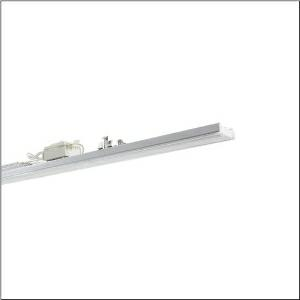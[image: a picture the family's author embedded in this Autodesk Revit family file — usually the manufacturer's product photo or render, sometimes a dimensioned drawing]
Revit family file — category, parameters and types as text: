
# Revit family: licross_21_recessed_ho_52tl12dn6e5m
name_source: partatom
category: Lighting Fixtures
units: mm (PartAtom-declared; Revit-internal decimal feet)

## family parameters
Cut with Voids When Loaded = No
Host = Face
Light Source = No
Part Type = Normal
Room Calculation Point = No
Round Connector Dimension = Use Diameter
Shared = No

## types (1)
- --- (1 x LED, 14610 lm, 84.6 W, 6500K)
    Apparent Load = 85 VA
    CIE Flux Codes = 69 91 98 100 100
    Color Rendering = 80
    Color Temperature = 6500K
    Default Elevation = 1800 mm
    Description = Licross 21 Recessed HO, luminaire insert, of sheet steel, galvanised, coil coated, white, length: 1.500mm, width: 66mm, height: 67mm, LED rated luminous flux: 14.610lm, light colour: 865, SDCM (Standard Deviation of Colour Matching)MacAdam ≤ 3 SDCM (initial), control gear: DALI 2, with plug, 5-pole, with phase selection, mains connection: 220..240V, AC, 50/60Hz, rated input power: 85W, internal wiring halogen-free, primary optical cover: cover, of PMMA, light emission: direct distribution, primary light characteristic: symmetric, protection rating (complete): IP40, insulation class (complete): insulation class I (protective earthing), certification: CE, ENEC, VDE, UKCA, protection symbol: D if used in an environment without relevant dust loads with corresponding accessories, impact resistance: IK06, permissible ambient temperature for indoor applications: -25..+30°C, corresponds to IFS (International Featured Standards) requirements for safety and quality in the food industry, reducing of maximum allowable ambient temperature of 5°C with ceiling mounting, LABS conformity tested according to VDMA 24364:2018-05, The light source and the operating device comply with the requirements of the Ecodesign Regulation (EU) 2019/2020 and are replaceable in accordance with this regulation, packaging unit: 1 piece
    Height = 58 mm
    Lamp = 1 x LED
    Lamp Light Flux = 14610 lm
    Lamp Power = 84.6 W
    Lamp count = 1
    Length = 1500 mm
    Luminous efficacy = 173 lm/W
    Manufacturer = Siteco
    ModVariant = No
    Model = 52TL12DN6E5M
    Mounting Place = Ceiling
    Mounting Type = Pendant
    Number of Poles = 1
    OnlyDefault = Yes
    Power Factor = 1
    Product Name = Licross 21 Recessed HO
    Product group = luminaire insert | ceiling pendant
    ProductGroupID = 901
    Protection Class = Protection class I
    Protection Degree = IP 40
    RLX_Detail_Level = 1
    RLX_Emergency_Light_Flux = 0 lm
    RLX_Emergency_Type = 0
    RLX_Emergency_Type_DB = No
    RlxData = <blob elided: 25001 chars, md5=13d18b7d>
    Socket = socket
    Standby Power = 0 W
    System Light Flux = 14610 lm
    System Power = 85 W
    Type Comments = factory setting: luminous flux: 100 % | dim-lin: 254 | 484 mA
    Type Image = l_1296930.jpg
    URL = http://relux.com
    VarID = @adj_092825
    Voltage = 0 V
    Weight = 0.00 kg
    Width = 66 mm

## geometry (parser evidence)
native form markers: Blend x4, Sweep x12
no freeform markers — native parametric forms only
